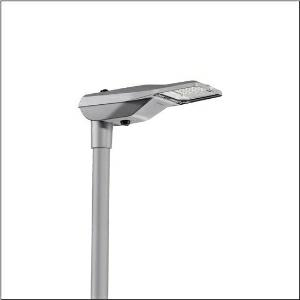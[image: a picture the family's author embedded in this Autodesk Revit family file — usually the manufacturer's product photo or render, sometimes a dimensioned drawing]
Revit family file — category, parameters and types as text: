
# Revit family: streetlight_sl_21_iq_micro___st1_0ab_5xe1m31y08cb_a08b
name_source: partatom
category: Lighting Fixtures
units: mm (PartAtom-declared; Revit-internal decimal feet)

## family parameters
Cut with Voids When Loaded = No
Host = Face
Light Source = No
Part Type = Normal
Room Calculation Point = No
Round Connector Dimension = Use Diameter
Shared = No

## types (1)
- --- (1 x LED, 2530 lm, 19.1 W, 3000K)
    Apparent Load = 19 VA
    CIE Flux Codes = 38 73 97 100 100
    Color Rendering = 70
    Color Temperature = 3000K
    Default Elevation = 1800 mm
    Description = Streetlight SL 21 iQ micro, mast luminaire, primary light control with lens, of PMMA, primary optical cover: cover, of toughened safety glass, transparent, light distribution: ST1.0aB, light emission: direct distribution, primary light characteristic: asymmetric, installation type: post-top, side-entry, LED, High Power LED, rated luminous flux: 2.530lm, luminous efficacy: 133lm/W, light colour: 730, colour temperature: 3000K, control gear: iQ-Street Remote, D4i with power reduction, control: pre-setting: logarithmic dimming characteristic, Street-Remote, Auto-Match, Temp-Guard, Lumen-Switch, Night-Set, Smart-Wire, Light-Fading, Desk-Remote (wireless, voltage-free reading and setting of iQ features in the workshop via application-optimized NFC function/RFID function), optimised constant luminous flux control (CLO 2.0), mains connection: 220..240V, AC, 50/60Hz, start of lifetime: 19W, end of service life: 20W, reduction: 9W, luminaire housing, of diecast aluminium, powder-coated, SITECO metallic grey (DB 702S), corrosivity category C5 high according to DIN EN ISO 12944, please order mast flange separately, inclination adjustable: 0°, 5°, 10°, 15°, sealing non-destructively replaceable, multi-level sealing system, length: 528mm, width: 235mm, height: 110mm, mast flange for spigot size: 42mm (side-entry): 5XC10008XM4, 60/48mm (side-entry/post-top): 5XC10108XM2, 76/60mm (side-entry/post-top): 5XC10108XM1, mounting height: 4..8m, Smart Interface below and above, protection rating (complete): IP66, insulation class (complete): insulation class II (safety insulation), certification: CE, ENEC, ENEC+, VDE, impact resistance: IK10, permissible operating ambient temperature for outdoor applications: -40..+50°C, standard-compliant lighting for roads and squares, packaging unit: 1 piece

Light Distribution: ST1.0aB
    Height = 110 mm
    Lamp = 1 x LED
    Lamp Light Flux = 2530 lm
    Lamp Power = 19.1 W
    Lamp count = 1
    Length = 528 mm
    Luminous efficacy = 132 lm/W
    Manufacturer = Siteco
    ModVariant = No
    Model = 5XE1M31Y08CB
    Number of Poles = 1
    OnlyDefault = Yes
    Power Factor = 1
    Product Name = Streetlight SL 21 iQ micro | ST1.0aB
    Product group = mast luminaire | pylon top
    ProductGroupID = 6100
    Protection Class = Protection class II
    Protection Degree = IP 66
    RLX_Detail_Level = 1
    RLX_Emergency_Light_Flux = 0 lm
    RLX_Emergency_Type = 0
    RLX_Emergency_Type_DB = No
    RlxData = <blob elided: 98709 chars, md5=a73e8dd2>
    Socket = socket
    Standby Power = 0 W
    System Light Flux = 2530 lm
    System Power = 19 W
    Type Comments = factory setting: luminous flux: 100 % | dim-lin: 254 | 387 mA
    Type Image = l_1007239.jpg
    URL = http://relux.com
    VarID = @adj_112663
    Voltage = 0 V
    Weight = 0.00 kg
    Width = 235 mm

## geometry (parser evidence)
native form markers: Blend x4, Sweep x11
no freeform markers — native parametric forms only
